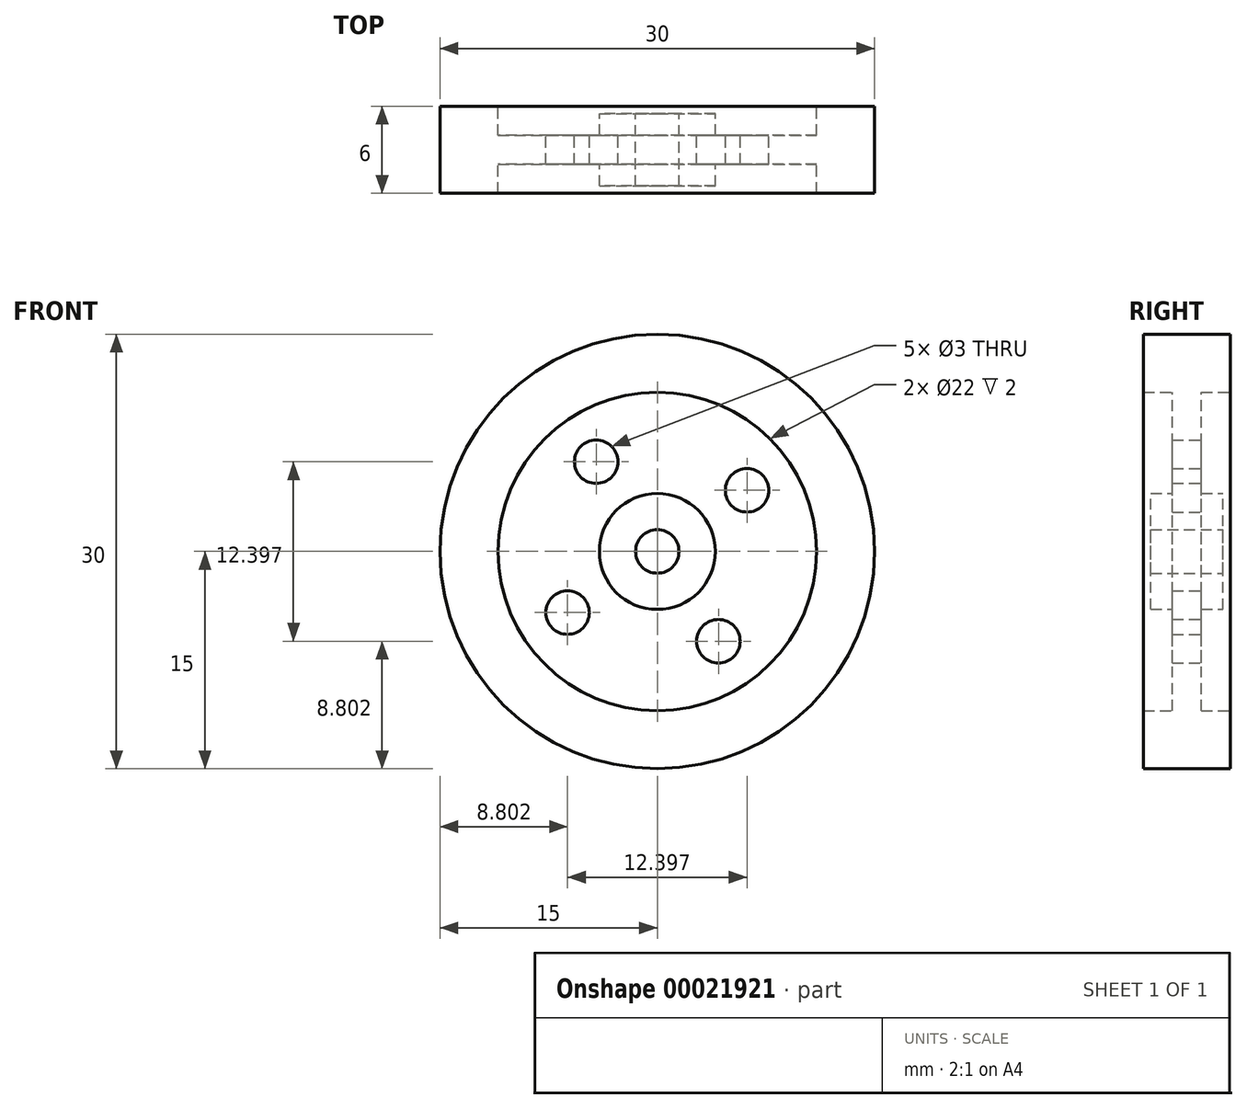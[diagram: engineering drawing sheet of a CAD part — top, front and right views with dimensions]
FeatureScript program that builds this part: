
annotation { "Feature Type Name" : "Feature", "Feature Type Description" : "" }
export const myFeature = defineFeature(function(context is Context, id is Id, definition is map)
    precondition{}
    {
        {
            var Q0;
            Q0=qCreatedBy(makeId("Front.planeOp"),FACE);
            var sketch = newSketch(context, id + "F0", { "sketchPlane" : qUnion([Q0])});
            skCircle(sketch, "E0", {"center": v(0, 0) * mm, "radius": 15 * mm});
            skCircle(sketch, "E1", {"center": v(0, 0) * mm, "radius": 1.5 * mm});
            skCircle(sketch, "E2", {"center": v(0, 0) * mm, "radius": 11 * mm});
            skCircle(sketch, "E3", {"center": v(-4.22, 6.2) * mm, "radius": 1.5 * mm});
            skCircle(sketch, "E4.1.0", {"center": v(-6.2, -4.22) * mm, "radius": 1.5 * mm});
            skCircle(sketch, "E4.2.0", {"center": v(4.22, -6.2) * mm, "radius": 1.5 * mm});
            skCircle(sketch, "E4.3.0", {"center": v(6.2, 4.22) * mm, "radius": 1.5 * mm});
            skCircle(sketch, "E5", {"center": v(0, 0) * mm, "radius": 4 * mm});
            skSolve(sketch);
        }
        {
            var Q0;
            Q0=makeQuery(id+"F0.imprint","IMPRINT",FACE,{"disambiguationData":[TD([[makeQuery(id+"F0.imprint","IMPRINT",EDGE,{"derivedFrom":sQuery(id+"F0.wireOp",EDGE,"E2")}),1.0]])]});
            extrude(context, id + "F1", {"entities" : qUnion([Q0]), "endBound" : BoundingType.SYMMETRIC, "depth" : 2 * mm});
        }
        {
            var Q0;
            Q0=makeQuery(id+"F0.imprint","IMPRINT",FACE,{"disambiguationData":[TD([[makeQuery(id+"F0.imprint","IMPRINT",EDGE,{"derivedFrom":sQuery(id+"F0.wireOp",EDGE,"E0")}),1.0]])]});
            extrude(context, id + "F2", {"entities" : qUnion([Q0]), "operationType" : NewBodyOperationType.ADD, "endBound" : BoundingType.SYMMETRIC, "depth" : 6 * mm});
        }
        {
            var Q0;
            Q0=makeQuery(id+"F0.imprint","IMPRINT",FACE,{"disambiguationData":[TD([[makeQuery(id+"F0.imprint","IMPRINT",EDGE,{"derivedFrom":sQuery(id+"F0.wireOp",EDGE,"E1")}),-1.0]])]});
            extrude(context, id + "F3", {"entities" : qUnion([Q0]), "operationType" : NewBodyOperationType.ADD, "endBound" : BoundingType.SYMMETRIC, "depth" : 5 * mm});
        }
    });
